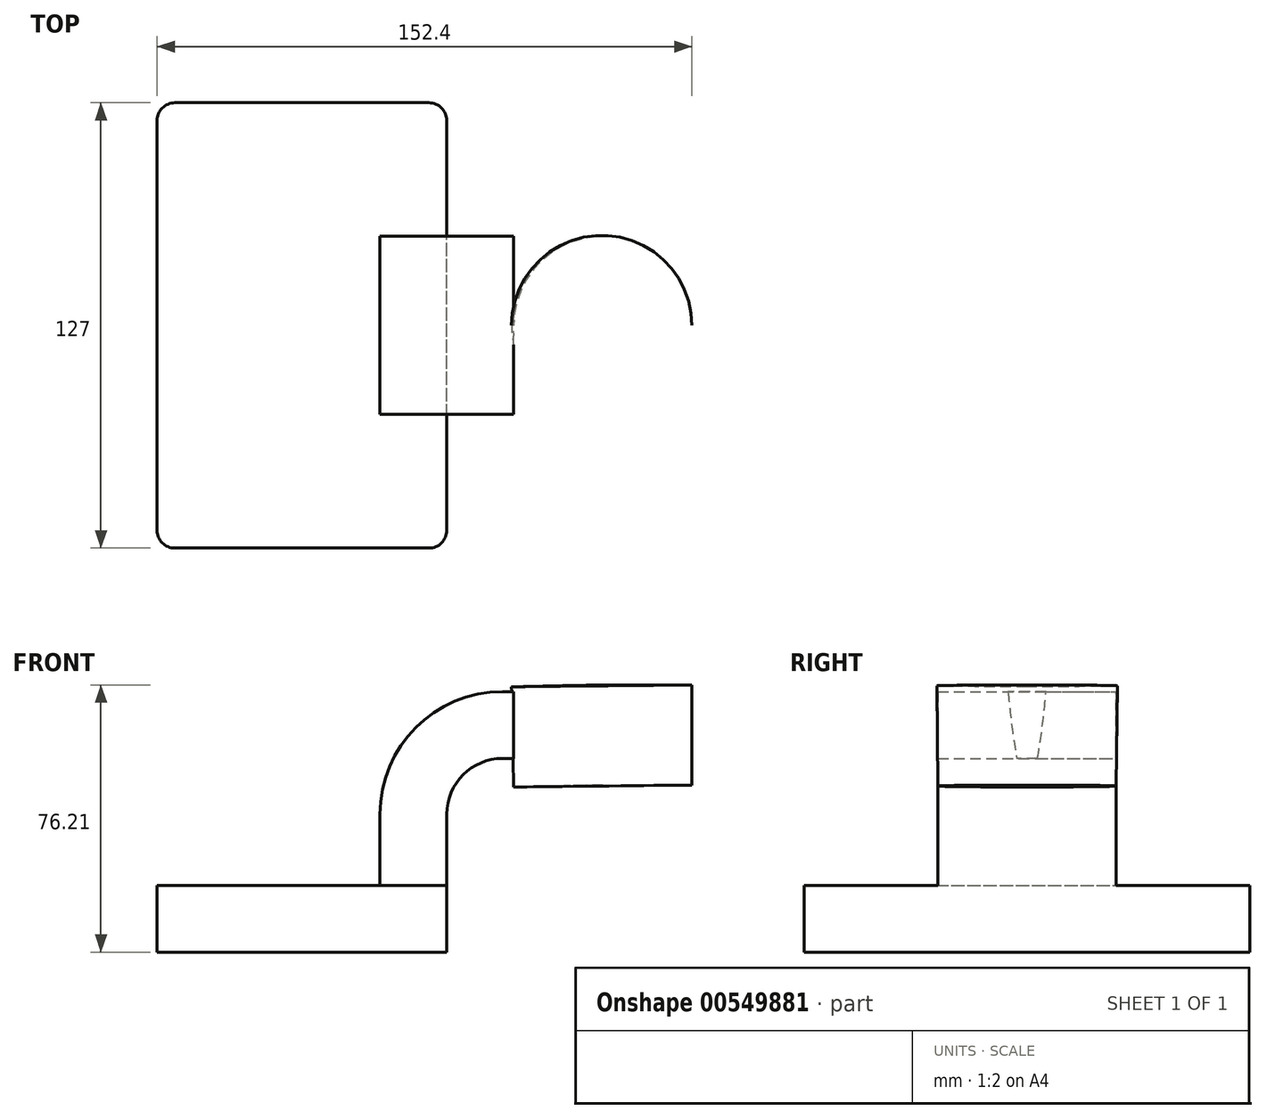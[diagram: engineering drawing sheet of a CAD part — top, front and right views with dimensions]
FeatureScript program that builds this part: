
annotation { "Feature Type Name" : "Feature", "Feature Type Description" : "" }
export const myFeature = defineFeature(function(context is Context, id is Id, definition is map)
    precondition{}
    {
        {
            var Q0;
            Q0=qCreatedBy(makeId("Front.planeOp"),FACE);
            var sketch = newSketch(context, id + "F0", { "sketchPlane" : qUnion([Q0])});
            skLineSegment(sketch, "E0.bottom", {"start": v(41.28, -9.52) * mm, "end": v(-41.28, -9.53) * mm});
            skLineSegment(sketch, "E0.top", {"start": v(41.28, 9.53) * mm, "end": v(-41.28, 9.53) * mm});
            skLineSegment(sketch, "E0.left", {"start": v(41.28, -9.52) * mm, "end": v(41.28, 9.53) * mm});
            skLineSegment(sketch, "E0.right", {"start": v(-41.28, -9.53) * mm, "end": v(-41.28, 9.53) * mm});
            skPoint(sketch, "E0.middle", {"position": v(0, 0) * mm});
            skLineSegment(sketch, "E1.bottom", {"start": v(111.12, 38.1) * mm, "end": v(60.32, 38.1) * mm});
            skLineSegment(sketch, "E1.top", {"start": v(111.12, 66.68) * mm, "end": v(60.32, 66.68) * mm});
            skLineSegment(sketch, "E1.left", {"start": v(111.12, 38.1) * mm, "end": v(111.12, 66.68) * mm});
            skLineSegment(sketch, "E1.right", {"start": v(60.32, 38.1) * mm, "end": v(60.32, 66.67) * mm});
            skPoint(sketch, "E1.middle", {"position": v(85.72, 52.39) * mm});
            skLineSegment(sketch, "E2", {"start": v(41.28, 9.53) * mm, "end": v(41.28, 29.82) * mm});
            skArc(sketch, "E3", {"start": v(41.27, 29.82) * mm, "mid": v(45.92, 41.04) * mm, "end": v(57.15, 45.7) * mm});
            skLineSegment(sketch, "E4", {"start": v(57.15, 45.7) * mm, "end": v(85.72, 45.7) * mm});
            skLineSegment(sketch, "E5.0", {"start": v(57.15, 64.74) * mm, "end": v(85.42, 64.74) * mm});
            skArc(sketch, "E5.1", {"start": v(22.23, 29.82) * mm, "mid": v(32.45, 54.51) * mm, "end": v(57.15, 64.74) * mm});
            skLineSegment(sketch, "E5.2", {"start": v(22.22, 9.53) * mm, "end": v(22.22, 29.82) * mm});
            skPoint(sketch, "E6", {"position": v(85.72, 38.1) * mm});
            skLineSegment(sketch, "E7", {"start": v(85.42, 66.68) * mm, "end": v(85.72, 38.1) * mm});
            skFitSpline(sketch, "E8", {"points": [v(-41.28, 9.52) * mm, v(57.15, 64.74) * mm], "startDerivative": vector(13.94, 22.36) * mm, "endDerivative": vector(113.03, -13.2) * mm});
            skSolve(sketch);
        }
        {
            var Q0;
            Q0=makeQuery(id+"F0.imprint","IMPRINT",FACE,{"disambiguationData":[TD([[makeQuery(id+"F0.imprint","IMPRINT",EDGE,{"derivedFrom":sQuery(id+"F0.wireOp",EDGE,"E0.bottom")}),-1.0]])]});
            extrude(context, id + "F1", {"entities" : qUnion([Q0]), "endBound" : BoundingType.SYMMETRIC, "depth" : 127 * mm, "offsetDistance" : 25.4 * mm});
        }
        {
            var Q0;
            {var subQ1=sQuery(id+"F0.wireOp",EDGE,"E2");Q0=makeQuery(id+"F0.imprint","IMPRINT",FACE,{"disambiguationData":[TD([[makeQuery(id+"F0.imprint","IMPRINT",EDGE,{"derivedFrom":subQ1}),1.0]])]});}
            extrude(context, id + "F2", {"entities" : qUnion([Q0]), "operationType" : NewBodyOperationType.ADD, "endBound" : BoundingType.SYMMETRIC, "depth" : 50.8 * mm, "offsetDistance" : 25.4 * mm});
        }
        {
            var Q0;
            Q0=makeQuery(id+"F0.imprint","IMPRINT",FACE,{"disambiguationData":[TD([[makeQuery(id+"F0.imprint","IMPRINT",EDGE,{"derivedFrom":sQuery(id+"F0.wireOp",EDGE,"E5.1")}),1.0]])]});
            extrude(context, id + "F3", {"entities" : qUnion([Q0]), "operationType" : NewBodyOperationType.ADD, "endBound" : BoundingType.SYMMETRIC, "depth" : 15.88 * mm, "offsetDistance" : 25.4 * mm});
        }
        {
            var Q0;
            {var subQ0=sQuery(id+"F0.wireOp",EDGE,"E1.left");Q0=makeQuery(id+"F0.imprint","IMPRINT",FACE,{"disambiguationData":[TD([[makeQuery(id+"F0.imprint","IMPRINT",EDGE,{"derivedFrom":subQ0}),1.0]])]});}
            var Q1;
            Q1=sQuery(id+"F0.wireOp",EDGE,"E7");
            revolve(context, id + "F4", {"operationType" : NewBodyOperationType.ADD, "entities" : qUnion([Q0]), "axis" : qUnion([Q1]), "revolveType" : RevolveType.FULL});
        }
        {
            var Q0;
            Q0=makeQuery(id+"F1.opExtrude","CAP_EDGE",EDGE,{"disambiguationData":[OSD([sQuery(id+"F0.wireOp",EDGE,"E0.left")])],"isStart":false});
            var Q1;
            Q1=makeQuery(id+"F1.opExtrude","CAP_EDGE",EDGE,{"disambiguationData":[OSD([sQuery(id+"F0.wireOp",EDGE,"E0.right")])],"isStart":false});
            var Q2;
            Q2=makeQuery(id+"F1.opExtrude","CAP_EDGE",EDGE,{"disambiguationData":[OSD([sQuery(id+"F0.wireOp",EDGE,"E0.right")])],"isStart":true});
            var Q3;
            Q3=makeQuery(id+"F1.opExtrude","CAP_EDGE",EDGE,{"disambiguationData":[OSD([sQuery(id+"F0.wireOp",EDGE,"E0.left")])],"isStart":true});
            fillet(context, id + "F5", {"entities" : qUnion([Q0, Q1, Q2, Q3]), "radius" : 5.08 * mm, "tangentPropagation" : true, "allowEdgeOverflow" : false});
        }
    });
